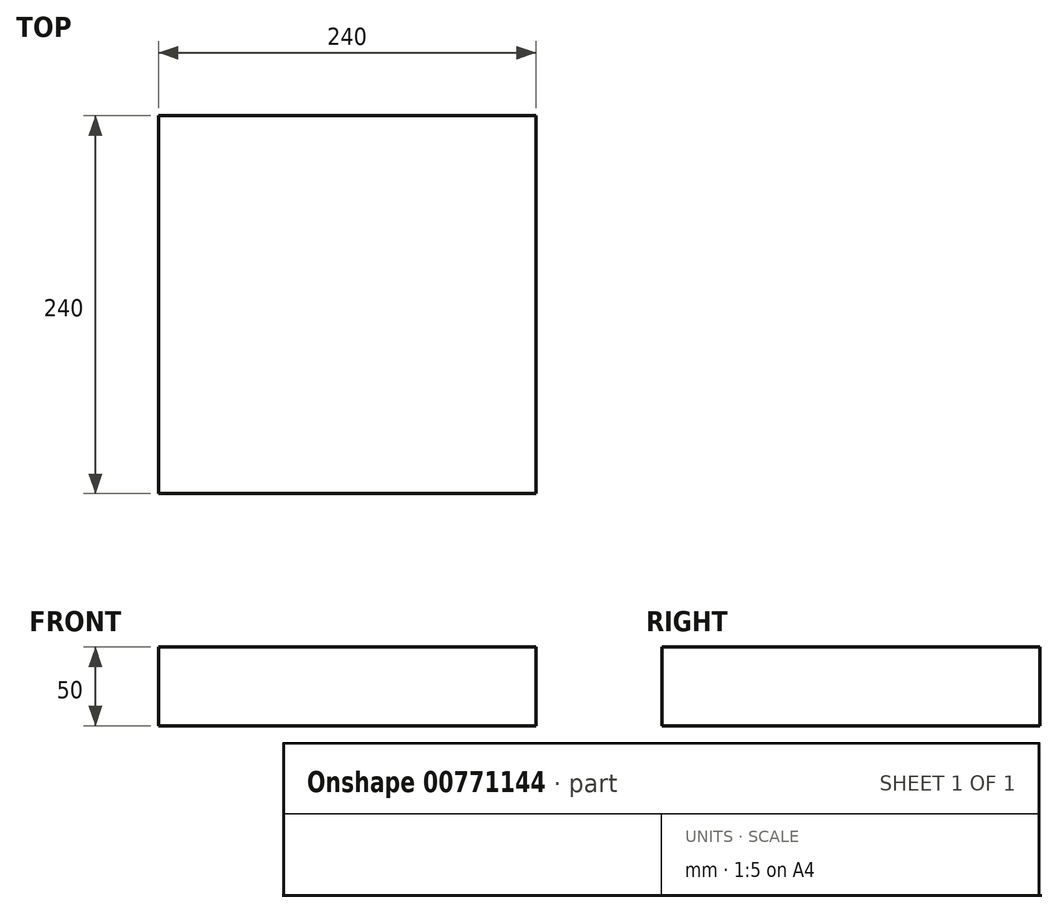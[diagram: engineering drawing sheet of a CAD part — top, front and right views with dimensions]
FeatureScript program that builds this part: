
annotation { "Feature Type Name" : "Feature", "Feature Type Description" : "" }
export const myFeature = defineFeature(function(context is Context, id is Id, definition is map)
    precondition{}
    {
        {
            var Q0;
            Q0=qCreatedBy(makeId("Top.planeOp"),FACE);
            var sketch = newSketch(context, id + "F0", { "sketchPlane" : qUnion([Q0])});
            skLineSegment(sketch, "E0.bottom", {"start": v(-120, 120) * mm, "end": v(120, 120) * mm});
            skLineSegment(sketch, "E0.top", {"start": v(-120, -120) * mm, "end": v(120, -120) * mm});
            skLineSegment(sketch, "E0.left", {"start": v(-120, 120) * mm, "end": v(-120, -120) * mm});
            skLineSegment(sketch, "E0.right", {"start": v(120, 120) * mm, "end": v(120, -120) * mm});
            skPoint(sketch, "E0.middle", {"position": v(0, 0) * mm});
            skSolve(sketch);
        }
        {
            var Q0;
            Q0=makeQuery(id+"F0.imprint","IMPRINT",FACE,{"disambiguationData":[TD([[makeQuery(id+"F0.imprint","IMPRINT",EDGE,{"derivedFrom":sQuery(id+"F0.wireOp",EDGE,"E0.bottom")}),-1.0]])]});
            extrude(context, id + "F1", {"entities" : qUnion([Q0]), "depth" : 50 * mm, "offsetDistance" : 25 * mm});
        }
    });
